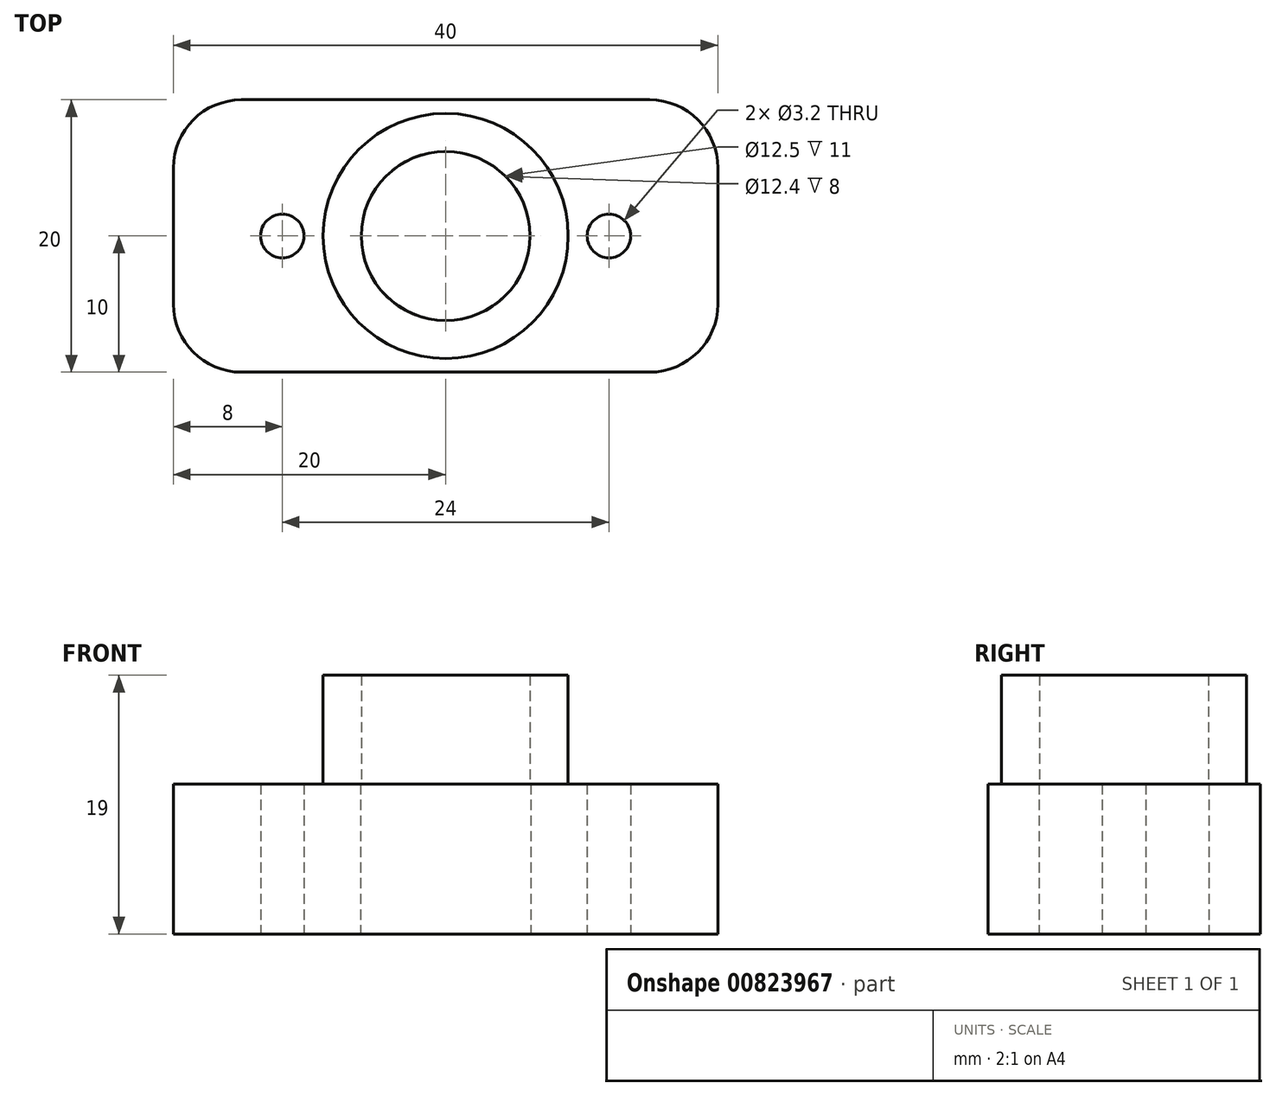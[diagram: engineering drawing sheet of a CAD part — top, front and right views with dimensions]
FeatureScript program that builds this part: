
annotation { "Feature Type Name" : "Feature", "Feature Type Description" : "" }
export const myFeature = defineFeature(function(context is Context, id is Id, definition is map)
    precondition{}
    {
        {
            var Q0;
            Q0=qCreatedBy(makeId("Top.planeOp"),FACE);
            var sketch = newSketch(context, id + "F0", { "sketchPlane" : qUnion([Q0])});
            skLineSegment(sketch, "E0.bottom", {"start": v(0, 0) * mm, "end": v(40, 0) * mm});
            skLineSegment(sketch, "E0.top", {"start": v(0, 20) * mm, "end": v(40, 20) * mm});
            skLineSegment(sketch, "E0.left", {"start": v(0, 0) * mm, "end": v(0, 20) * mm});
            skLineSegment(sketch, "E0.right", {"start": v(40, 0) * mm, "end": v(40, 20) * mm});
            skCircle(sketch, "E1", {"center": v(20, 10) * mm, "radius": 6.25 * mm});
            skPoint(sketch, "E1.centerSnap0", {"position": v(0, 10) * mm});
            skPoint(sketch, "E1.centerSnap1", {"position": v(20, 0) * mm});
            skCircle(sketch, "E2", {"center": v(32, 10) * mm, "radius": 1.6 * mm});
            skCircle(sketch, "E3", {"center": v(8, 10) * mm, "radius": 1.6 * mm});
            skSolve(sketch);
        }
        {
            var Q0;
            Q0 = qSketchRegion(id + "F0", true);
            extrude(context, id + "F1", {"entities" : qUnion([Q0]), "depth" : 11 * mm, "offsetDistance" : 25 * mm});
        }
        {
            var Q0;
            Q0=makeQuery(id+"F1.opExtrude","CAP_FACE",FACE,{"disambiguationData":[OSD([sQuery(id+"F0.wireOp",EDGE,"E0.bottom"),sQuery(id+"F0.wireOp",EDGE,"E0.top"),sQuery(id+"F0.wireOp",EDGE,"E0.left"),sQuery(id+"F0.wireOp",EDGE,"E0.right"),sQuery(id+"F0.wireOp",EDGE,"E1"),sQuery(id+"F0.wireOp",EDGE,"E2"),sQuery(id+"F0.wireOp",EDGE,"E3")])],"isStart":false});
            var sketch = newSketch(context, id + "F2", { "sketchPlane" : qUnion([Q0])});
            skCircle(sketch, "E4", {"center": v(20, 10) * mm, "radius": 6.2 * mm});
            skCircle(sketch, "E5", {"center": v(20, 10) * mm, "radius": 9 * mm});
            skSolve(sketch);
        }
        {
            var Q0;
            Q0 = qSketchRegion(id + "F2", true);
            extrude(context, id + "F3", {"entities" : qUnion([Q0]), "operationType" : NewBodyOperationType.ADD, "depth" : 8 * mm, "offsetDistance" : 25 * mm});
        }
        {
            var Q0;
            Q0=makeQuery(id+"F1.opExtrude","SWEPT_EDGE",EDGE,{"disambiguationData":[OSD([sQuery(id+"F0.wireOp",EDGE,"E0.top"),sQuery(id+"F0.wireOp",EDGE,"E0.right")])]});
            var Q1;
            Q1=makeQuery(id+"F1.opExtrude","SWEPT_EDGE",EDGE,{"disambiguationData":[OSD([sQuery(id+"F0.wireOp",EDGE,"E0.bottom"),sQuery(id+"F0.wireOp",EDGE,"E0.right")])]});
            var Q2;
            Q2=makeQuery(id+"F1.opExtrude","SWEPT_EDGE",EDGE,{"disambiguationData":[OSD([sQuery(id+"F0.wireOp",EDGE,"E0.bottom"),sQuery(id+"F0.wireOp",EDGE,"E0.left")])]});
            var Q3;
            Q3=makeQuery(id+"F1.opExtrude","SWEPT_EDGE",EDGE,{"disambiguationData":[OSD([sQuery(id+"F0.wireOp",EDGE,"E0.top"),sQuery(id+"F0.wireOp",EDGE,"E0.left")])]});
            fillet(context, id + "F4", {"entities" : qUnion([Q0, Q1, Q2, Q3]), "radius" : 5 * mm, "tangentPropagation" : true, "allowEdgeOverflow" : false});
        }
    });
